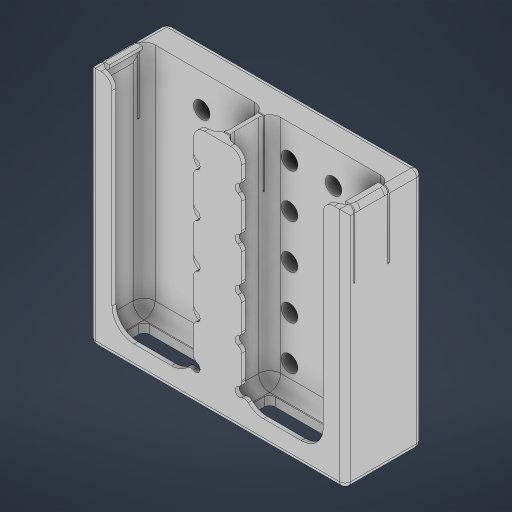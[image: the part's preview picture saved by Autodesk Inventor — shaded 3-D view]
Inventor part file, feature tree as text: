
AUTODESK INVENTOR PART (.ipt)
format: ipt  version: 2023 (Build 270158000, 158)  size: 579,584 bytes
history: native  units: in
note: dims shown in document units (in); Inventor stores cm internally (conversion verified against a paired STEP export)
features: extrude x7, sketch x7, fillet x5, mirror x1, hole x1, pattern_linear x1, projected_geometry x1
ambient origin geometry x8: Origin, YZ Plane, XZ Plane, XY Plane, X Axis, Y Axis, Z Axis, Center Point
bodies: Solid1 (feature_tree)
feature tree (23):
  extrude  "Extrusion1"  Depth=5.3in
  extrude  "Extrusion2"  Depth=1.75in TaperAngle=0.0deg
  extrude  "Extrusion3"  Depth=0.09in
  fillet  "Fillet1"  Radius=0.09in
  extrude  "Extrusion4"  Depth=5.3in TaperAngle=0.0deg
  extrude  "Extrusion5"  Depth=0.5in
  mirror  "Mirror1"
  extrude  "Extrusion6"  Depth=0.2in TaperAngle=0.0deg
  fillet  "Fillet2"  Radius=0.25in
  fillet  "Fillet3"  Radius=0.2in
  fillet  "Fillet4"  Radius=0.025in
  hole  "Hole2"  [1 undecoded]
  pattern_linear  "Rectangular Pattern2"  Spacing1=1.5in  [1 undecoded]
  extrude  "Extrusion7"  TaperAngle=0.0deg  [1 undecoded]
  fillet  "Fillet5"  Radius=1.0in
  sketch  "Sketch1"  dims[d0=5.61in d1=5.3in]
  sketch  "Sketch2"  dims[d2=0.1in d3=1.75in d4=0.0in]
  sketch  "Sketch3"  dims[d5=0.09in d6=0.09in d7=0.09in]
  sketch  "Sketch4"  dims[d8=1.05in d9=5.3in d10=0.0in]
  sketch  "Sketch5"  dims[d11=0.5in d12=0.5in]
  projected_geometry  "Projected Loop2"
  sketch  "Sketch8"  dims[d13=0.5in d14=5.25in d15=0.0in d16=0.25in d17=0.2in d18=0.025in]
  sketch  "Sketch9"  dims[d19=0.025in d20=0.75in d21=1.5in d22=0.0in d23=0.0in d30=1.0in d31=0.0in d32=0.125in d33=0.05in d35=0.375in d36=0.355in d37=0.025in d39=1.0in d40=0.0in d57=0.5in d58=0.25in d59=0.125in d60=2.77in d61=2.77in d62=0.5in d63=0.5in d64=0.09in d65=0.025in d66=0.025in d67=0.025in d68=0.5in d69=1.0in d70=1.0in d71=0.5in d72=1.0in d73=1.0in d74=1.0in d75=1.0in d76=1.0in d77=1.0in d78=0.201in d79=0.75in d80=0.375in d81=0.25in d82=0.5635in d83=1.0in d84=0.8108in d85=1.5748in d87=1.0in d88=1.9685in d90=1.0in d91=1.0in d92=0.0in d93=0.125in]
note: 3 required parameter values undecoded (feature->parameter linkage not recoverable at this tier; creation-order binding heuristic only, values carry confidence <= 0.55)
